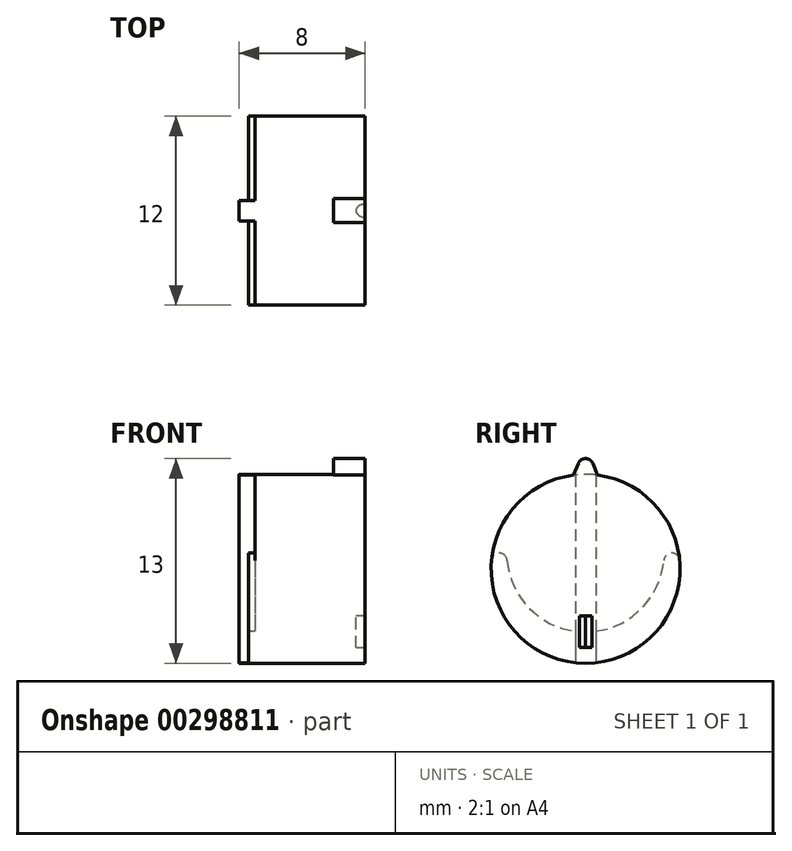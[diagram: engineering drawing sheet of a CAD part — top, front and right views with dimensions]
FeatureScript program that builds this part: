
annotation { "Feature Type Name" : "Feature", "Feature Type Description" : "" }
export const myFeature = defineFeature(function(context is Context, id is Id, definition is map)
    precondition{}
    {
        {
            var Q0;
            Q0=qCreatedBy(makeId("Front.planeOp"),FACE);
            var sketch = newSketch(context, id + "F0", { "sketchPlane" : qUnion([Q0])});
            skLineSegment(sketch, "E0", {"start": v(41, 5) * mm, "end": v(41, 7.5) * mm});
            skLineSegment(sketch, "E1", {"start": v(41, 5) * mm, "end": v(45, 5) * mm});
            skLineSegment(sketch, "E2", {"start": v(45, 5) * mm, "end": v(45, 0) * mm});
            skLineSegment(sketch, "E3", {"start": v(45, 0) * mm, "end": v(0, 0) * mm});
            skLineSegment(sketch, "E4", {"start": v(0, 0) * mm, "end": v(0, 9.5) * mm});
            skLineSegment(sketch, "E5", {"start": v(-10.7, 0) * mm, "end": v(55.74, 0) * mm, "construction": true});
            skLineSegment(sketch, "E6", {"start": v(41, 7.5) * mm, "end": v(32, 7.5) * mm});
            skLineSegment(sketch, "E7", {"start": v(32, 8.5) * mm, "end": v(32, 7.5) * mm});
            skLineSegment(sketch, "E8", {"start": v(32, 8.5) * mm, "end": v(8, 8.5) * mm});
            skLineSegment(sketch, "E9", {"start": v(8, 8.5) * mm, "end": v(8, 9.5) * mm});
            skLineSegment(sketch, "E10", {"start": v(8, 9.5) * mm, "end": v(0, 9.5) * mm});
            skSolve(sketch);
        }
        {
            var Q0;
            Q0=makeQuery(id+"F0.imprint","IMPRINT",FACE,{"disambiguationData":[TD([[makeQuery(id+"F0.imprint","IMPRINT",EDGE,{"derivedFrom":sQuery(id+"F0.wireOp",EDGE,"E0")}),1.0]])]});
            var Q1;
            Q1=sQuery(id+"F0.wireOp",EDGE,"E5");
            revolve(context, id + "F1", {"entities" : qUnion([Q0]), "axis" : qUnion([Q1]), "revolveType" : RevolveType.FULL});
        }
        {
            var Q0;
            Q0=makeQuery(id+"F1.opRevolve","SWEPT_FACE",FACE,{"disambiguationData":[OSD([sQuery(id+"F0.wireOp",EDGE,"E2")])]});
            var sketch = newSketch(context, id + "F2", { "sketchPlane" : qUnion([Q0])});
            skCircle(sketch, "E11", {"center": v(0, -1) * mm, "radius": 6 * mm});
            skSolve(sketch);
        }
        {
            var Q0;
            Q0=makeQuery(id+"F2.imprint","IMPRINT",FACE,{"disambiguationData":[TD([[makeQuery(id+"F2.imprint","IMPRINT",EDGE,{"derivedFrom":sQuery(id+"F2.wireOp",EDGE,"E11")}),1.0]])]});
            var Q1;
            Q1=makeQuery(id+"F2.imprint","IMPRINT",FACE,{"disambiguationData":[TD([[makeQuery(id+"F2.imprint","IMPRINT",EDGE,{"derivedFrom":makeQuery(id+"F1.opRevolve","SWEPT_EDGE",EDGE,{"disambiguationData":[OSD([sQuery(id+"F0.wireOp",EDGE,"E1"),sQuery(id+"F0.wireOp",EDGE,"E2")])]})}),-1.0]])]});
            extrude(context, id + "F3", {"entities" : qUnion([Q0, Q1]), "operationType" : NewBodyOperationType.ADD, "depth" : 7 * mm});
        }
        {
            var Q0;
            Q0=makeQuery(id+"F3.opExtrude","CAP_FACE",FACE,{"disambiguationData":[OSD([sQuery(id+"F2.wireOp",EDGE,"E11")])],"isStart":false});
            var sketch = newSketch(context, id + "F4", { "sketchPlane" : qUnion([Q0])});
            skLineSegment(sketch, "E12", {"start": v(-0.77, 4.95) * mm, "end": v(-0.46, 5.7) * mm});
            skLineSegment(sketch, "E13", {"start": v(0.46, 5.7) * mm, "end": v(0.77, 4.95) * mm});
            skPoint(sketch, "E14.visualSharp", {"position": v(0, 6.8) * mm});
            skArc(sketch, "E14.filletArc", {"start": v(0.46, 5.7) * mm, "mid": v(0, 6) * mm, "end": v(-0.46, 5.7) * mm});
            skSolve(sketch);
        }
        {
            var Q0;
            {var subQ0=sQuery(id+"F4.wireOp",EDGE,"E12");Q0=makeQuery(id+"F4.imprint","IMPRINT",FACE,{"disambiguationData":[TD([[makeQuery(id+"F4.imprint","IMPRINT",EDGE,{"derivedFrom":subQ0}),-1.0]])]});}
            extrude(context, id + "F5", {"entities" : qUnion([Q0]), "operationType" : NewBodyOperationType.ADD, "oppositeDirection" : true, "depth" : 2 * mm});
        }
        {
            var Q0;
            Q0=makeQuery(id+"F1.opRevolve","SWEPT_EDGE",EDGE,{"disambiguationData":[OSD([sQuery(id+"F0.wireOp",EDGE,"E6"),sQuery(id+"F0.wireOp",EDGE,"E7")])]});
            var Q1;
            Q1=makeQuery(id+"F1.opRevolve","SWEPT_EDGE",EDGE,{"disambiguationData":[OSD([sQuery(id+"F0.wireOp",EDGE,"E0"),sQuery(id+"F0.wireOp",EDGE,"E1")])]});
            var Q2;
            Q2=makeQuery(id+"F1.opRevolve","SWEPT_EDGE",EDGE,{"disambiguationData":[OSD([sQuery(id+"F0.wireOp",EDGE,"E8"),sQuery(id+"F0.wireOp",EDGE,"E9")])]});
            fillet(context, id + "F6", {"entities" : qUnion([Q0, Q1, Q2]), "radius" : 0.5 * mm, "tangentPropagation" : true, "allowEdgeOverflow" : false});
        }
        {
            var Q0;
            {var subQ0=sQuery(id+"F4.wireOp",EDGE,"E14.filletArc");var subQ1=sQuery(id+"F4.wireOp",EDGE,"E13");var subQ2=sQuery(id+"F4.wireOp",EDGE,"E12");var subQ3=sQuery(id+"F2.wireOp",EDGE,"E11");Q0=makeQuery(id+"F9gwVez07aFZszp_1.7.F5.boolean.opBoolean","MERGE",FACE,{"derivedFrom":[makeQuery(id+"F9gwVez07aFZszp_1.6.F5.boolean.opBoolean","MERGE",FACE,{"derivedFrom":[makeQuery(id+"F9gwVez07aFZszp_1.5.F5.boolean.opBoolean","MERGE",FACE,{"derivedFrom":[makeQuery(id+"F9gwVez07aFZszp_1.4.F5.boolean.opBoolean","MERGE",FACE,{"derivedFrom":[makeQuery(id+"F9gwVez07aFZszp_1.3.F5.boolean.opBoolean","MERGE",FACE,{"derivedFrom":[makeQuery(id+"F9gwVez07aFZszp_1.2.F5.boolean.opBoolean","MERGE",FACE,{"derivedFrom":[makeQuery(id+"F9gwVez07aFZszp_1.1.F5.boolean.opBoolean","MERGE",FACE,{"derivedFrom":[makeQuery(id+"F5.boolean.opBoolean","MERGE",FACE,{"derivedFrom":[makeQuery(id+"F3.opExtrude","CAP_FACE",FACE,{"disambiguationData":[OSD([subQ3])],"isStart":false}),makeQuery(id+"F5.opExtrude","CAP_FACE",FACE,{"disambiguationData":[OSD([subQ3,subQ2,subQ1,subQ0])],"isStart":true})]}),makeQuery(id+"F9gwVez07aFZszp_1.1.F5.opExtrude","CAP_FACE",FACE,{"disambiguationData":[OSD([subQ3,subQ2,subQ1,subQ0])],"isStart":true})]}),makeQuery(id+"F9gwVez07aFZszp_1.2.F5.opExtrude","CAP_FACE",FACE,{"disambiguationData":[OSD([subQ3,subQ2,subQ1,subQ0])],"isStart":true})]}),makeQuery(id+"F9gwVez07aFZszp_1.3.F5.opExtrude","CAP_FACE",FACE,{"disambiguationData":[OSD([subQ3,subQ2,subQ1,subQ0])],"isStart":true})]}),makeQuery(id+"F9gwVez07aFZszp_1.4.F5.opExtrude","CAP_FACE",FACE,{"disambiguationData":[OSD([subQ3,subQ2,subQ1,subQ0])],"isStart":true})]}),makeQuery(id+"F9gwVez07aFZszp_1.5.F5.opExtrude","CAP_FACE",FACE,{"disambiguationData":[OSD([subQ3,subQ2,subQ1,subQ0])],"isStart":true})]}),makeQuery(id+"F9gwVez07aFZszp_1.6.F5.opExtrude","CAP_FACE",FACE,{"disambiguationData":[OSD([subQ3,subQ2,subQ1,subQ0])],"isStart":true})]}),makeQuery(id+"F9gwVez07aFZszp_1.7.F5.opExtrude","CAP_FACE",FACE,{"disambiguationData":[OSD([subQ3,subQ2,subQ1,subQ0])],"isStart":true})]});}
            var sketch = newSketch(context, id + "F7", { "sketchPlane" : qUnion([Q0])});
            skLineSegment(sketch, "E15.bottom", {"start": v(-0.4, -6) * mm, "end": v(0.4, -6) * mm});
            skLineSegment(sketch, "E15.top", {"start": v(-0.4, -4) * mm, "end": v(0.4, -4) * mm});
            skLineSegment(sketch, "E15.left", {"start": v(-0.4, -6) * mm, "end": v(-0.4, -4) * mm});
            skLineSegment(sketch, "E15.right", {"start": v(0.4, -6) * mm, "end": v(0.4, -4) * mm});
            skPoint(sketch, "E15.middle", {"position": v(0, -5) * mm});
            skSolve(sketch);
        }
        {
            var Q0;
            Q0=makeQuery(id+"F7.imprint","IMPRINT",FACE,{"disambiguationData":[TD([[makeQuery(id+"F7.imprint","IMPRINT",EDGE,{"derivedFrom":sQuery(id+"F7.wireOp",EDGE,"E15.bottom")}),1.0]])]});
            extrude(context, id + "F8", {"entities" : qUnion([Q0]), "operationType" : NewBodyOperationType.REMOVE, "oppositeDirection" : true, "depth" : 0.6 * mm});
        }
        {
            var Q0;
            Q0=makeQuery(id+"F8.boolean.opBoolean","COPY",EDGE,{"derivedFrom":makeQuery(id+"F8.opExtrude","CAP_EDGE",EDGE,{"disambiguationData":[OSD([sQuery(id+"F7.wireOp",EDGE,"E15.right")])],"isStart":false})});
            var Q1;
            Q1=makeQuery(id+"F8.boolean.opBoolean","COPY",EDGE,{"derivedFrom":makeQuery(id+"F8.opExtrude","CAP_EDGE",EDGE,{"disambiguationData":[OSD([sQuery(id+"F7.wireOp",EDGE,"E15.left")])],"isStart":false})});
            fillet(context, id + "F9", {"entities" : qUnion([Q0, Q1]), "radius" : 0.5 * mm, "tangentPropagation" : true, "allowEdgeOverflow" : false});
        }
        {
            var Q0;
            Q0=qCreatedBy(makeId("Front.planeOp"),FACE);
            var sketch = newSketch(context, id + "F10", { "sketchPlane" : qUnion([Q0])});
            skLineSegment(sketch, "E16.bottom", {"start": v(45, 19) * mm, "end": v(-45, 19) * mm});
            skLineSegment(sketch, "E16.top", {"start": v(45, -19) * mm, "end": v(-45, -19) * mm});
            skLineSegment(sketch, "E16.left", {"start": v(45, 19) * mm, "end": v(45, -19) * mm});
            skLineSegment(sketch, "E16.right", {"start": v(-45, 19) * mm, "end": v(-45, -19) * mm});
            skPoint(sketch, "E16.middle", {"position": v(0, 0) * mm});
            skSolve(sketch);
        }
        {
            var Q0;
            Q0=makeQuery(id+"F10.imprint","IMPRINT",FACE,{"disambiguationData":[TD([[makeQuery(id+"F10.imprint","IMPRINT",EDGE,{"derivedFrom":sQuery(id+"F10.wireOp",EDGE,"E16.bottom")}),1.0]])]});
            extrude(context, id + "F11", {"entities" : qUnion([Q0]), "operationType" : NewBodyOperationType.REMOVE, "depth" : 50 * mm, "hasSecondDirection" : true, "secondDirectionOppositeDirection" : true, "secondDirectionDepth" : 50 * mm});
        }
        {
            var Q0;
            Q0=makeQuery(id+"F11.boolean.opBoolean","MERGE",FACE,{"derivedFrom":[makeQuery(id+"F3.opExtrude","CAP_FACE",FACE,{"disambiguationData":[OSD([sQuery(id+"F2.wireOp",EDGE,"E11")])],"isStart":true}),makeQuery(id+"F11.opExtrude","SWEPT_FACE",FACE,{"disambiguationData":[OSD([sQuery(id+"F10.wireOp",EDGE,"E16.left")])]})]});
            var sketch = newSketch(context, id + "F12", { "sketchPlane" : qUnion([Q0])});
            skLineSegment(sketch, "E17.left", {"start": v(-0.65, 4.96) * mm, "end": v(-0.65, -6.96) * mm});
            skLineSegment(sketch, "E17.right", {"start": v(0.65, 4.96) * mm, "end": v(0.65, -6.96) * mm});
            skPoint(sketch, "E17.middle", {"position": v(0, -1) * mm});
            skSolve(sketch);
        }
        {
            var Q0;
            {var subQ0=sQuery(id+"F12.wireOp",EDGE,"E17.left");Q0=makeQuery(id+"F12.imprint","IMPRINT",FACE,{"disambiguationData":[TD([[makeQuery(id+"F12.imprint","IMPRINT",EDGE,{"derivedFrom":subQ0}),1.0]])]});}
            extrude(context, id + "F13", {"entities" : qUnion([Q0]), "operationType" : NewBodyOperationType.ADD, "depth" : 1 * mm});
        }
        {
            var Q0;
            {var subQ0=sQuery(id+"F2.wireOp",EDGE,"E11");var subQ1=sQuery(id+"F12.wireOp",EDGE,"E17.right");Q0=makeQuery(id+"F13.boolean.opBoolean","SPLIT",FACE,{"disambiguationData":[TD([makeQuery(id+"F13.opExtrude","SWEPT_FACE",FACE,{"disambiguationData":[OSD([subQ1])]})])],"derivedFrom":makeQuery(id+"F11.boolean.opBoolean","MERGE",FACE,{"derivedFrom":[makeQuery(id+"F3.opExtrude","CAP_FACE",FACE,{"disambiguationData":[OSD([subQ0])],"isStart":true}),makeQuery(id+"F11.opExtrude","SWEPT_FACE",FACE,{"disambiguationData":[OSD([sQuery(id+"F10.wireOp",EDGE,"E16.left")])]})]})});}
            var sketch = newSketch(context, id + "F14", { "sketchPlane" : qUnion([Q0])});
            skArc(sketch, "E18", {"start": v(-5, 0) * mm, "mid": v(0, -5) * mm, "end": v(5, 0) * mm});
            skArc(sketch, "E19", {"start": v(-5.92, 0) * mm, "mid": v(0, -7) * mm, "end": v(5.92, 0) * mm});
            skLineSegment(sketch, "E20", {"start": v(-5.92, 0) * mm, "end": v(-5, 0) * mm});
            skLineSegment(sketch, "E21.MirrorCS", {"start": v(5.92, 0) * mm, "end": v(5, 0) * mm});
            skSolve(sketch);
        }
        {
            var Q0;
            {var subQ0=sQuery(id+"F14.wireOp",EDGE,"E20");Q0=makeQuery(id+"F14.imprint","IMPRINT",FACE,{"disambiguationData":[TD([[makeQuery(id+"F14.imprint","IMPRINT",EDGE,{"derivedFrom":subQ0}),-1.0]])]});}
            var Q1;
            {var subQ0=sQuery(id+"F14.wireOp",EDGE,"E21.MirrorCS");Q1=makeQuery(id+"F14.imprint","IMPRINT",FACE,{"disambiguationData":[TD([[makeQuery(id+"F14.imprint","IMPRINT",EDGE,{"derivedFrom":subQ0}),1.0]])]});}
            extrude(context, id + "F15", {"entities" : qUnion([Q0, Q1]), "operationType" : NewBodyOperationType.ADD, "depth" : 0.4 * mm});
        }
        {
            var Q0;
            Q0=makeQuery(id+"F15.opExtrude","SWEPT_EDGE",EDGE,{"disambiguationData":[OSD([sQuery(id+"F14.wireOp",EDGE,"E18"),sQuery(id+"F14.wireOp",EDGE,"E20")])]});
            var Q1;
            Q1=makeQuery(id+"F15.opExtrude","SWEPT_EDGE",EDGE,{"disambiguationData":[OSD([sQuery(id+"F14.wireOp",EDGE,"E19"),sQuery(id+"F14.wireOp",EDGE,"E20")])]});
            var Q2;
            Q2=makeQuery(id+"F15.opExtrude","SWEPT_EDGE",EDGE,{"disambiguationData":[OSD([sQuery(id+"F14.wireOp",EDGE,"E18"),sQuery(id+"F14.wireOp",EDGE,"E21.MirrorCS")])]});
            var Q3;
            Q3=makeQuery(id+"F15.opExtrude","SWEPT_EDGE",EDGE,{"disambiguationData":[OSD([sQuery(id+"F2.wireOp",EDGE,"E11"),sQuery(id+"F14.wireOp",EDGE,"E19"),sQuery(id+"F14.wireOp",EDGE,"E21.MirrorCS")])]});
            fillet(context, id + "F16", {"entities" : qUnion([Q0, Q1, Q2, Q3]), "radius" : 0.5 * mm, "tangentPropagation" : true, "allowEdgeOverflow" : false});
        }
    });
